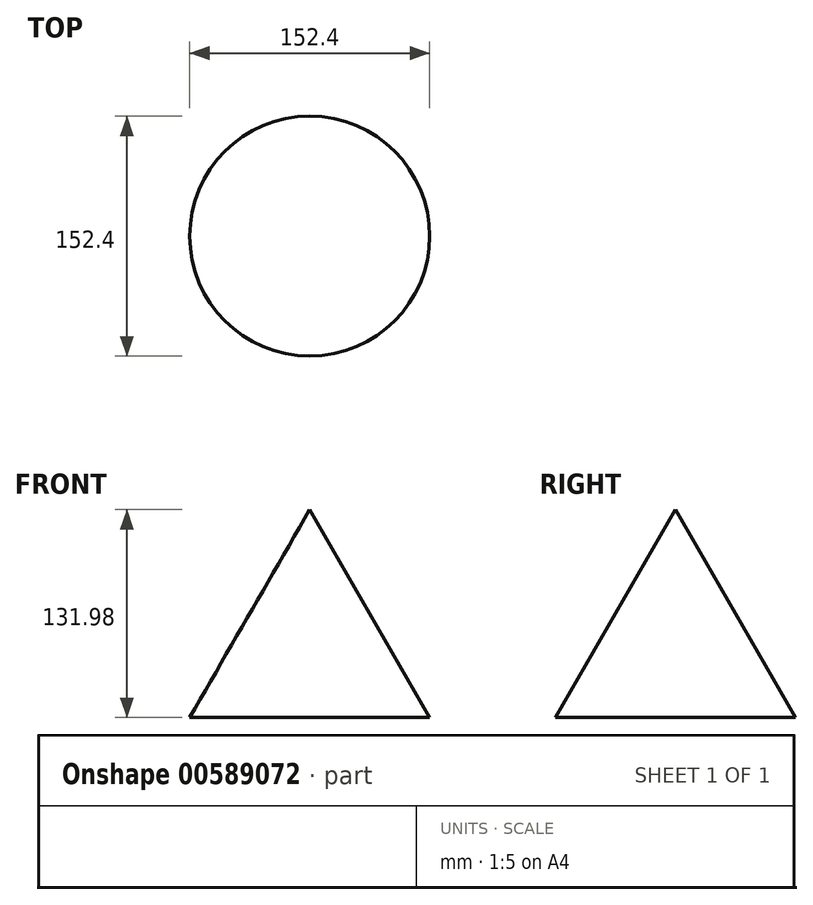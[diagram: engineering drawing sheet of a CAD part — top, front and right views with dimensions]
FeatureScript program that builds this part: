
annotation { "Feature Type Name" : "Feature", "Feature Type Description" : "" }
export const myFeature = defineFeature(function(context is Context, id is Id, definition is map)
    precondition{}
    {
        {
            var Q0;
            Q0=qCreatedBy(makeId("Front.planeOp"),FACE);
            var sketch = newSketch(context, id + "F0", { "sketchPlane" : qUnion([Q0])});
            skLineSegment(sketch, "E0", {"start": v(0, 131.98) * mm, "end": v(76.2, 0) * mm});
            skLineSegment(sketch, "E1", {"start": v(76.2, 0) * mm, "end": v(0, 0) * mm});
            skLineSegment(sketch, "E2", {"start": v(0, 131.98) * mm, "end": v(0, 0) * mm});
            skSolve(sketch);
        }
        {
            var Q0;
            Q0=makeQuery(id+"F0.imprint","IMPRINT",FACE,{"disambiguationData":[TD([[makeQuery(id+"F0.imprint","IMPRINT",EDGE,{"derivedFrom":sQuery(id+"F0.wireOp",EDGE,"E0")}),-1.0]])]});
            var Q1;
            Q1=sQuery(id+"F0.wireOp",EDGE,"E2");
            revolve(context, id + "F1", {"entities" : qUnion([Q0]), "axis" : qUnion([Q1]), "revolveType" : RevolveType.FULL});
        }
    });
